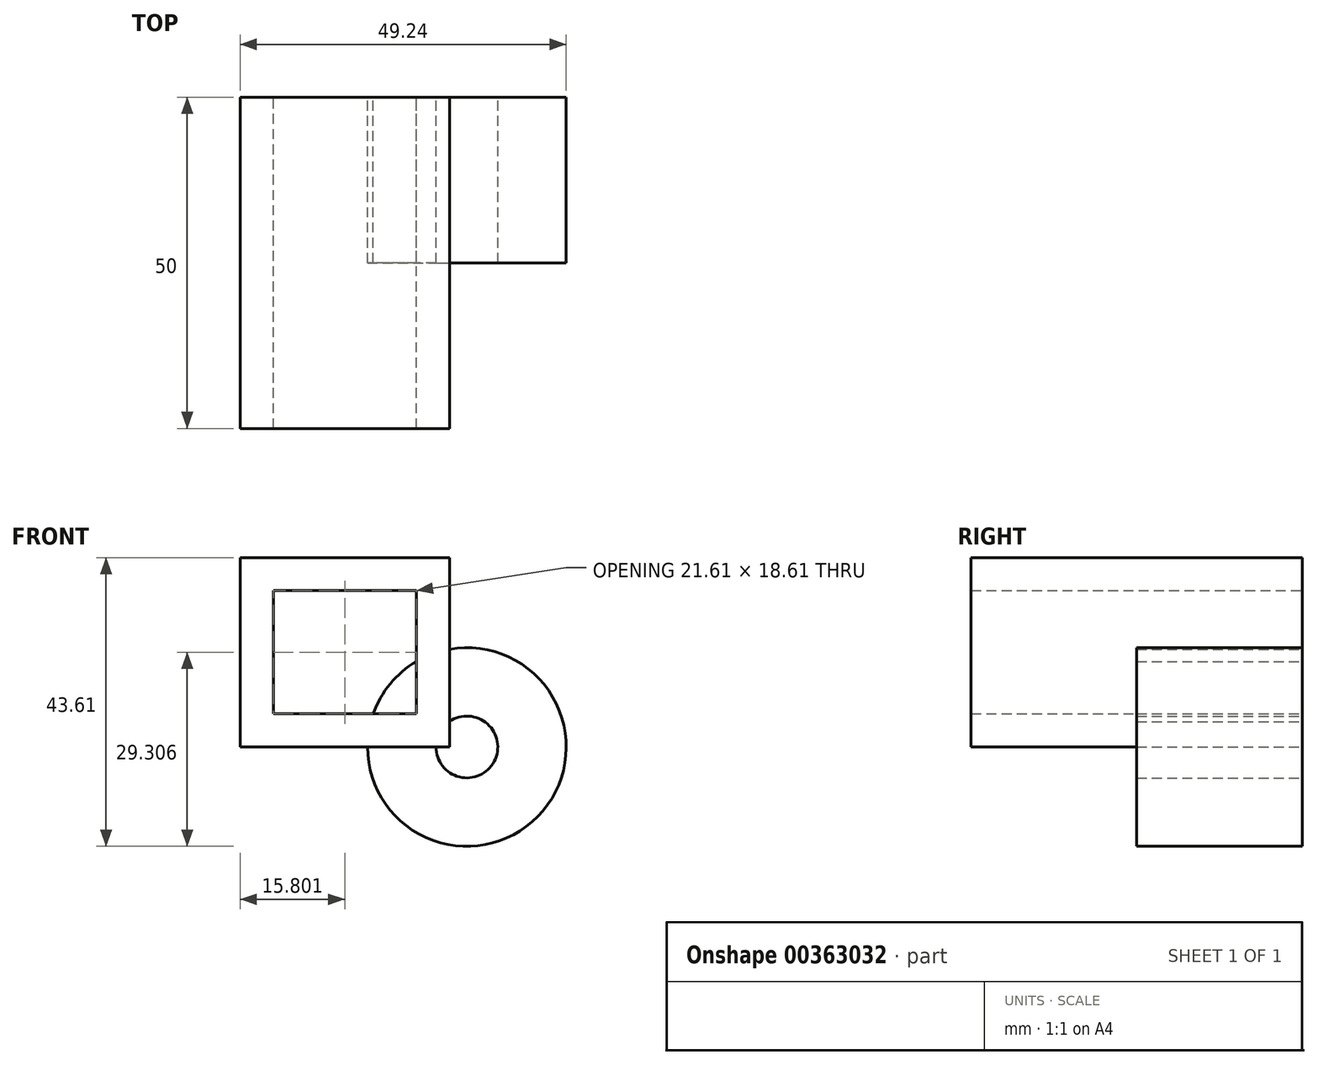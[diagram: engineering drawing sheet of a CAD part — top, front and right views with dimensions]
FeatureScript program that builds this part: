
annotation { "Feature Type Name" : "Feature", "Feature Type Description" : "" }
export const myFeature = defineFeature(function(context is Context, id is Id, definition is map)
    precondition{}
    {
        {
            var Q0;
            Q0=qCreatedBy(makeId("Front.planeOp"),FACE);
            var sketch = newSketch(context, id + "F0", { "sketchPlane" : qUnion([Q0])});
            skCircle(sketch, "E0", {"center": v(0, 0) * mm, "radius": 15 * mm});
            skCircle(sketch, "E1", {"center": v(0, 0) * mm, "radius": 4.67 * mm});
            skSolve(sketch);
        }
        {
            var Q0;
            Q0=qCreatedBy(makeId("Front.planeOp"),FACE);
            var sketch = newSketch(context, id + "F1", { "sketchPlane" : qUnion([Q0])});
            skLineSegment(sketch, "E2.bottom", {"start": v(-2.63, 0) * mm, "end": v(-34.24, 0) * mm});
            skLineSegment(sketch, "E2.top", {"start": v(-2.63, 28.61) * mm, "end": v(-34.24, 28.61) * mm});
            skLineSegment(sketch, "E2.left", {"start": v(-2.63, 0) * mm, "end": v(-2.63, 28.61) * mm});
            skLineSegment(sketch, "E2.right", {"start": v(-34.24, 0) * mm, "end": v(-34.24, 28.61) * mm});
            skLineSegment(sketch, "E3.0", {"start": v(-29.24, 5) * mm, "end": v(-29.24, 23.61) * mm});
            skLineSegment(sketch, "E3.1", {"start": v(-7.63, 5) * mm, "end": v(-29.24, 5) * mm});
            skLineSegment(sketch, "E3.2", {"start": v(-7.63, 5) * mm, "end": v(-7.63, 23.61) * mm});
            skLineSegment(sketch, "E3.3", {"start": v(-7.63, 23.61) * mm, "end": v(-29.24, 23.61) * mm});
            skSolve(sketch);
        }
        {
            var Q0;
            Q0=makeQuery(id+"F1.imprint","IMPRINT",FACE,{"disambiguationData":[TD([[makeQuery(id+"F1.imprint","IMPRINT",EDGE,{"derivedFrom":sQuery(id+"F1.wireOp",EDGE,"E2.bottom")}),-1.0]])]});
            extrude(context, id + "F2", {"entities" : qUnion([Q0]), "depth" : 25 * mm});
        }
        {
            var Q0;
            Q0=makeQuery(id+"F2.opExtrude","CAP_FACE",FACE,{"disambiguationData":[OSD([sQuery(id+"F1.wireOp",EDGE,"E2.bottom"),sQuery(id+"F1.wireOp",EDGE,"E2.top"),sQuery(id+"F1.wireOp",EDGE,"E2.left"),sQuery(id+"F1.wireOp",EDGE,"E2.right")])],"isStart":false});
            var Q1;
            Q1=makeQuery(id+"F0.imprint","IMPRINT",FACE,{"disambiguationData":[TD([[makeQuery(id+"F0.imprint","IMPRINT",EDGE,{"derivedFrom":sQuery(id+"F0.wireOp",EDGE,"E0")}),1.0]])]});
            extrude(context, id + "F3", {"entities" : qUnion([Q0, Q1]), "operationType" : NewBodyOperationType.ADD, "depth" : 25 * mm});
        }
    });
